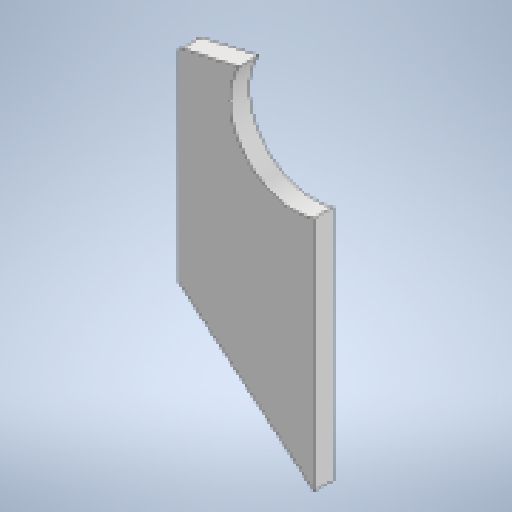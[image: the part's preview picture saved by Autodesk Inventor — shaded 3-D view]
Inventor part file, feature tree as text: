
AUTODESK INVENTOR PART (.ipt)
format: ipt  version: 2023 (Build 270158000, 158)  size: 431,104 bytes
history: native  units: in
note: dims shown in document units (in); Inventor stores cm internally (conversion verified against a paired STEP export)
features: extrude x16, sketch x16, other x11, projected_geometry x10, reference x1
ambient origin geometry x8: Origin, YZ Plane, XZ Plane, XY Plane, X Axis, Y Axis, Z Axis, Center Point
bodies: Body1 (feature_tree)
feature tree (54):
  other  "Bryła1"
  extrude  "Wyciągnięcie proste1"  Depth=0.3436in
  extrude  "Wyciągnięcie proste2"  Depth=0.1969in TaperAngle=0.0deg
  other  "Płaszczyzna konstrukcyjna1"
  extrude  "Wyciągnięcie proste3"  Depth=0.1969in
  extrude  "Wyciągnięcie proste4"  TaperAngle=0.0deg  [1 undecoded]
  extrude  "Wyciągnięcie proste5"  Depth=0.3937in TaperAngle=0.0deg
  sketch  "Szkic6"
  other  "Płaszczyzna konstrukcyjna2"
  extrude  "Wyciągnięcie proste6"  Depth=0.3937in TaperAngle=0.0deg
  extrude  "Wyciągnięcie proste7"  TaperAngle=45.0deg  [1 undecoded]
  extrude  "Wyciągnięcie proste8"  TaperAngle=0.0deg  [1 undecoded]
  extrude  "Wyciągnięcie proste9"  Depth=0.0787in
  extrude  "Wyciągnięcie proste10"  Depth=0.2165in
  extrude  "Wyciągnięcie proste11"  Depth=0.0787in
  extrude  "Wyciągnięcie proste12"  Depth=0.5512in
  extrude  "Wyciągnięcie proste13"  Depth=0.1181in
  extrude  "Wyciągnięcie proste14"  Depth=0.2165in
  other  "Edytuj bezpośrednio1"
  extrude  "Wyciągnięcie proste15"  Depth=0.3937in TaperAngle=0.0deg
  extrude  "Wyciągnięcie proste16"  Depth=0.1181in
  other  "Edytuj bezpośrednio2"
  sketch  "Szkic1"
  reference  "Odniesienie1"
  sketch  "Szkic2"
  projected_geometry  "Pętla rzutowana1"
  sketch  "Szkic3"
  projected_geometry  "Pętla rzutowana2"
  sketch  "Szkic4"
  projected_geometry  "Pętla rzutowana3"
  sketch  "Szkic5"
  projected_geometry  "Pętla rzutowana4"
  sketch  "Szkic7"
  sketch  "Szkic8"
  projected_geometry  "Pętla rzutowana5"
  sketch  "Szkic9"
  sketch  "Szkic10"
  sketch  "Szkic11"
  projected_geometry  "Pętla rzutowana6"
  sketch  "Szkic12"
  projected_geometry  "Pętla rzutowana7"
  sketch  "Szkic13"
  projected_geometry  "Pętla rzutowana8"
  sketch  "Szkic14"
  projected_geometry  "Pętla rzutowana9"
  sketch  "Szkic15"
  sketch  "Szkic16"
  projected_geometry  "Pętla rzutowana10"
  other  "Zespół2"
  other  "sciana_lewa_v5:1"
  other  "Przesuń1"
  other  "Przesuń2"
  other  "Zespół3"
  other  "minisumopodsr:1"
note: 3 required parameter values undecoded (feature->parameter linkage not recoverable at this tier; creation-order binding heuristic only, values carry confidence <= 0.55)
